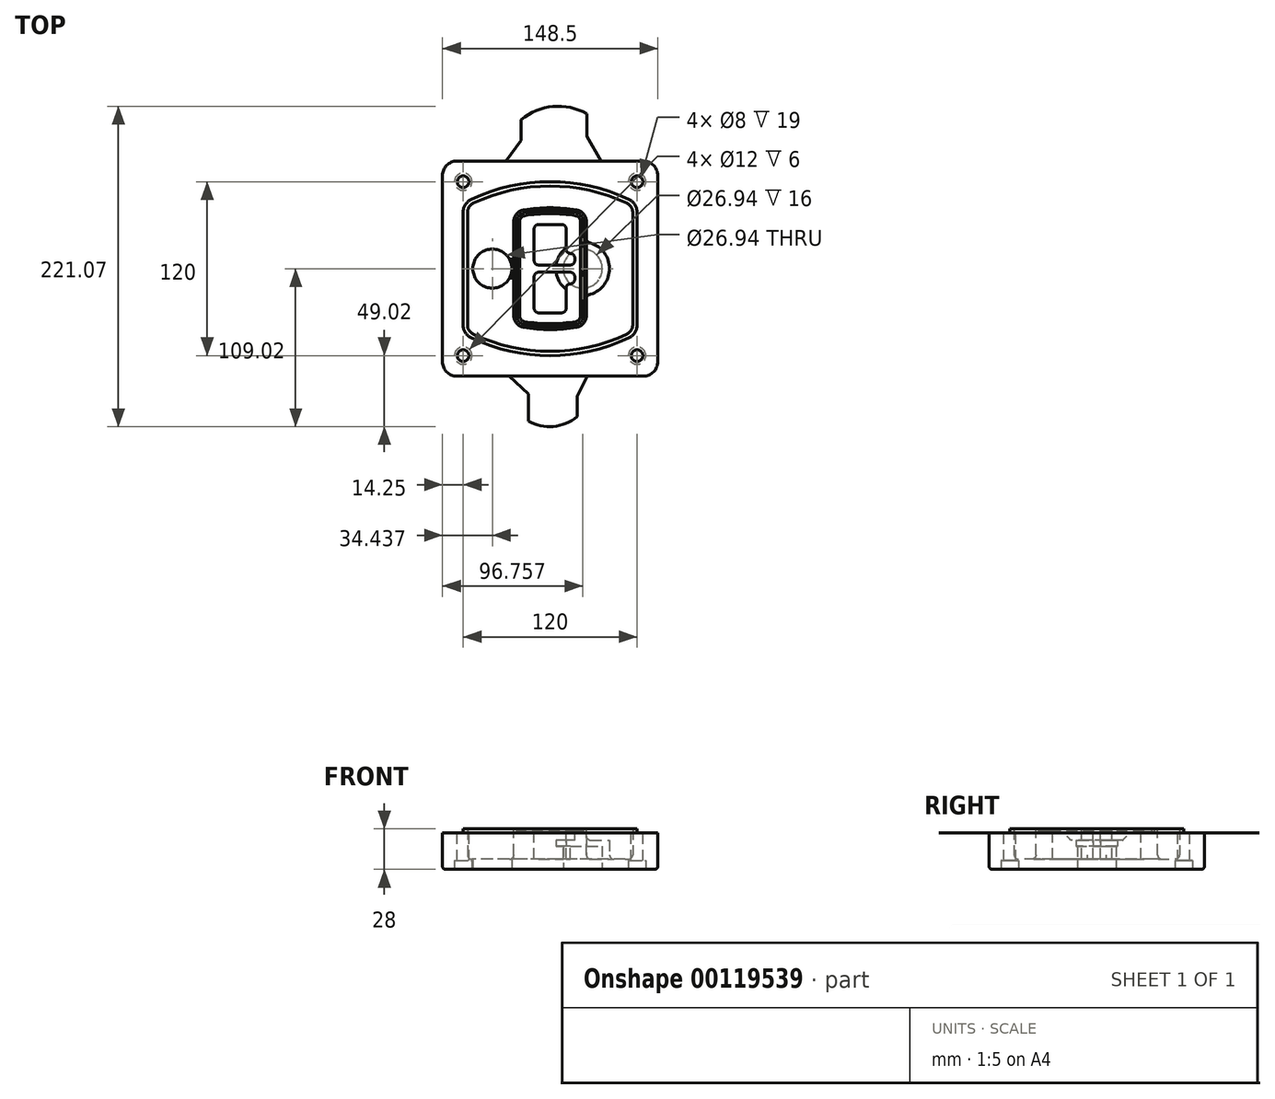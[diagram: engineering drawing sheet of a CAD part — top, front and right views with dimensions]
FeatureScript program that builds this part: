
annotation { "Feature Type Name" : "Feature", "Feature Type Description" : "" }
export const myFeature = defineFeature(function(context is Context, id is Id, definition is map)
    precondition{}
    {
        {
            var Q0;
            Q0=qCreatedBy(makeId("Top.planeOp"),FACE);
            var sketch = newSketch(context, id + "F0", { "sketchPlane" : qUnion([Q0])});
            skPoint(sketch, "E0.rect.middle", {"position": v(0, 0) * mm});
            skLineSegment(sketch, "E1.bottom", {"start": v(-64.25, -74.25) * mm, "end": v(64.25, -74.25) * mm});
            skLineSegment(sketch, "E1.top", {"start": v(-64.25, 74.25) * mm, "end": v(64.25, 74.25) * mm});
            skLineSegment(sketch, "E1.left", {"start": v(-74.25, -64.25) * mm, "end": v(-74.25, 64.25) * mm});
            skLineSegment(sketch, "E1.right", {"start": v(74.25, -64.25) * mm, "end": v(74.25, 64.25) * mm});
            skLineSegment(sketch, "E2", {"start": v(-74.25, 74.25) * mm, "end": v(74.25, -74.25) * mm, "construction": true});
            skLineSegment(sketch, "E3", {"start": v(74.25, 74.25) * mm, "end": v(-74.25, -74.25) * mm, "construction": true});
            skCircle(sketch, "E4", {"center": v(-60, 60) * mm, "radius": 4 * mm});
            skCircle(sketch, "E5", {"center": v(60, 60) * mm, "radius": 4 * mm});
            skCircle(sketch, "E6", {"center": v(60, -60) * mm, "radius": 4 * mm});
            skCircle(sketch, "E7", {"center": v(-60, -60) * mm, "radius": 4 * mm});
            skLineSegment(sketch, "E8", {"start": v(-60, 60) * mm, "end": v(60, 60) * mm, "construction": true});
            skLineSegment(sketch, "E9", {"start": v(60, 60) * mm, "end": v(60, -60) * mm, "construction": true});
            skLineSegment(sketch, "E10", {"start": v(60, -60) * mm, "end": v(-60, -60) * mm, "construction": true});
            skLineSegment(sketch, "E11", {"start": v(-60, -60) * mm, "end": v(-60, 60) * mm, "construction": true});
            skLineSegment(sketch, "E12", {"start": v(-60, 38.83) * mm, "end": v(-60, -38.83) * mm});
            skLineSegment(sketch, "E13", {"start": v(60, 38.83) * mm, "end": v(60, -38.83) * mm});
            skArc(sketch, "E14", {"start": v(54.26, 47.88) * mm, "mid": v(0, 60) * mm, "end": v(-54.26, 47.88) * mm});
            skArc(sketch, "E15", {"start": v(-54.26, -47.88) * mm, "mid": v(0, -60) * mm, "end": v(54.26, -47.88) * mm});
            skLineSegment(sketch, "E16", {"start": v(-60, 0) * mm, "end": v(60, 0) * mm, "construction": true});
            skPoint(sketch, "E17.visualSharp", {"position": v(-60, -45) * mm});
            skArc(sketch, "E17.filletArc", {"start": v(-60, -38.83) * mm, "mid": v(-58.44, -44.2) * mm, "end": v(-54.26, -47.88) * mm});
            skPoint(sketch, "E18.visualSharp", {"position": v(-60, 45) * mm});
            skArc(sketch, "E18.filletArc", {"start": v(-54.26, 47.88) * mm, "mid": v(-58.44, 44.2) * mm, "end": v(-60, 38.83) * mm});
            skPoint(sketch, "E19.visualSharp", {"position": v(60, 45) * mm});
            skArc(sketch, "E19.filletArc", {"start": v(60, 38.83) * mm, "mid": v(58.44, 44.2) * mm, "end": v(54.26, 47.88) * mm});
            skPoint(sketch, "E20.visualSharp", {"position": v(60, -45) * mm});
            skArc(sketch, "E20.filletArc", {"start": v(54.26, -47.88) * mm, "mid": v(58.44, -44.2) * mm, "end": v(60, -38.83) * mm});
            skPoint(sketch, "E21.visualSharp", {"position": v(-74.25, 74.25) * mm});
            skArc(sketch, "E21.filletArc", {"start": v(-64.25, 74.25) * mm, "mid": v(-71.32, 71.32) * mm, "end": v(-74.25, 64.25) * mm});
            skPoint(sketch, "E22.visualSharp", {"position": v(74.25, 74.25) * mm});
            skArc(sketch, "E22.filletArc", {"start": v(74.25, 64.25) * mm, "mid": v(71.32, 71.32) * mm, "end": v(64.25, 74.25) * mm});
            skPoint(sketch, "E23.visualSharp", {"position": v(74.25, -74.25) * mm});
            skArc(sketch, "E23.filletArc", {"start": v(64.25, -74.25) * mm, "mid": v(71.32, -71.32) * mm, "end": v(74.25, -64.25) * mm});
            skPoint(sketch, "E24.visualSharp", {"position": v(-74.25, -74.25) * mm});
            skArc(sketch, "E24.filletArc", {"start": v(-74.25, -64.25) * mm, "mid": v(-71.32, -71.32) * mm, "end": v(-64.25, -74.25) * mm});
            skArc(sketch, "E25.0", {"start": v(57, 38.83) * mm, "mid": v(55.9, 42.58) * mm, "end": v(52.98, 45.17) * mm});
            skLineSegment(sketch, "E25.1", {"start": v(57, 38.83) * mm, "end": v(57, -38.83) * mm});
            skArc(sketch, "E25.2", {"start": v(52.98, -45.17) * mm, "mid": v(55.9, -42.58) * mm, "end": v(57, -38.83) * mm});
            skArc(sketch, "E25.3", {"start": v(-52.98, -45.17) * mm, "mid": v(0, -57) * mm, "end": v(52.98, -45.17) * mm});
            skArc(sketch, "E25.4", {"start": v(-57, -38.83) * mm, "mid": v(-55.9, -42.58) * mm, "end": v(-52.98, -45.17) * mm});
            skArc(sketch, "E25.5", {"start": v(52.98, 45.17) * mm, "mid": v(0, 57) * mm, "end": v(-52.98, 45.17) * mm});
            skLineSegment(sketch, "E25.6", {"start": v(-57, 38.83) * mm, "end": v(-57, -38.83) * mm});
            skArc(sketch, "E25.7", {"start": v(-52.98, 45.17) * mm, "mid": v(-55.9, 42.58) * mm, "end": v(-57, 38.83) * mm});
            skArc(sketch, "E26.0", {"start": v(-55.96, 51.5) * mm, "mid": v(-61.82, 46.33) * mm, "end": v(-64, 38.83) * mm});
            skArc(sketch, "E26.1", {"start": v(55.96, 51.5) * mm, "mid": v(0, 64) * mm, "end": v(-55.96, 51.5) * mm});
            skArc(sketch, "E26.2", {"start": v(64, 38.83) * mm, "mid": v(61.82, 46.33) * mm, "end": v(55.96, 51.5) * mm});
            skLineSegment(sketch, "E26.3", {"start": v(64, 38.83) * mm, "end": v(64, -38.83) * mm});
            skArc(sketch, "E26.4", {"start": v(55.96, -51.5) * mm, "mid": v(61.82, -46.33) * mm, "end": v(64, -38.83) * mm});
            skLineSegment(sketch, "E26.5", {"start": v(-64, 38.83) * mm, "end": v(-64, -38.83) * mm});
            skArc(sketch, "E26.6", {"start": v(-55.96, -51.5) * mm, "mid": v(0, -64) * mm, "end": v(55.96, -51.5) * mm});
            skArc(sketch, "E26.7", {"start": v(-64, -38.83) * mm, "mid": v(-61.82, -46.33) * mm, "end": v(-55.96, -51.5) * mm});
            skSolve(sketch);
        }
        {
            var Q0;
            Q0=makeQuery(id+"F0.imprint","IMPRINT",FACE,{"disambiguationData":[TD([[makeQuery(id+"F0.imprint","IMPRINT",EDGE,{"derivedFrom":sQuery(id+"F0.wireOp",EDGE,"E1.bottom")}),1.0]])]});
            var Q1;
            Q1=makeQuery(id+"F0.imprint","IMPRINT",FACE,{"disambiguationData":[TD([[makeQuery(id+"F0.imprint","IMPRINT",EDGE,{"derivedFrom":sQuery(id+"F0.wireOp",EDGE,"E12")}),1.0]])]});
            var Q2;
            Q2=makeQuery(id+"F0.imprint","IMPRINT",FACE,{"disambiguationData":[TD([[makeQuery(id+"F0.imprint","IMPRINT",EDGE,{"derivedFrom":sQuery(id+"F0.wireOp",EDGE,"E25.0")}),1.0]])]});
            var Q3;
            Q3=makeQuery(id+"F0.imprint","IMPRINT",FACE,{"disambiguationData":[TD([[makeQuery(id+"F0.imprint","IMPRINT",EDGE,{"derivedFrom":sQuery(id+"F0.wireOp",EDGE,"E12")}),-1.0]])]});
            extrude(context, id + "F1", {"entities" : qUnion([Q0, Q1, Q2, Q3]), "oppositeDirection" : true, "depth" : 25 * mm});
        }
        {
            var Q0;
            Q0=makeQuery(id+"F0.imprint","IMPRINT",FACE,{"disambiguationData":[TD([[makeQuery(id+"F0.imprint","IMPRINT",EDGE,{"derivedFrom":sQuery(id+"F0.wireOp",EDGE,"E12")}),1.0]])]});
            extrude(context, id + "F2", {"entities" : qUnion([Q0]), "operationType" : NewBodyOperationType.ADD, "depth" : 3 * mm});
        }
        {
            var Q0;
            Q0=makeQuery(id+"F0.imprint","IMPRINT",FACE,{"disambiguationData":[TD([[makeQuery(id+"F0.imprint","IMPRINT",EDGE,{"derivedFrom":sQuery(id+"F0.wireOp",EDGE,"E25.0")}),1.0]])]});
            extrude(context, id + "F3", {"entities" : qUnion([Q0]), "operationType" : NewBodyOperationType.REMOVE, "oppositeDirection" : true, "depth" : 18 * mm});
        }
        {
            var Q0;
            Q0=makeQuery(id+"F2.opExtrude","CAP_FACE",FACE,{"disambiguationData":[OSD([sQuery(id+"F0.wireOp",EDGE,"E12"),sQuery(id+"F0.wireOp",EDGE,"E13"),sQuery(id+"F0.wireOp",EDGE,"E14"),sQuery(id+"F0.wireOp",EDGE,"E15"),sQuery(id+"F0.wireOp",EDGE,"E17.filletArc"),sQuery(id+"F0.wireOp",EDGE,"E18.filletArc"),sQuery(id+"F0.wireOp",EDGE,"E19.filletArc"),sQuery(id+"F0.wireOp",EDGE,"E20.filletArc"),sQuery(id+"F0.wireOp",EDGE,"E25.0"),sQuery(id+"F0.wireOp",EDGE,"E25.1"),sQuery(id+"F0.wireOp",EDGE,"E25.2"),sQuery(id+"F0.wireOp",EDGE,"E25.3"),sQuery(id+"F0.wireOp",EDGE,"E25.4"),sQuery(id+"F0.wireOp",EDGE,"E25.5"),sQuery(id+"F0.wireOp",EDGE,"E25.6"),sQuery(id+"F0.wireOp",EDGE,"E25.7")])],"isStart":false});
            var sketch = newSketch(context, id + "F4", { "sketchPlane" : qUnion([Q0])});
            skArc(sketch, "E27.0", {"start": v(-18.34, -40.45) * mm, "mid": v(0, -42) * mm, "end": v(18.34, -40.45) * mm});
            skArc(sketch, "E28.0", {"start": v(18.34, 40.45) * mm, "mid": v(0, 42) * mm, "end": v(-18.34, 40.45) * mm});
            skLineSegment(sketch, "E29", {"start": v(-25, 32.57) * mm, "end": v(-25, -32.57) * mm});
            skLineSegment(sketch, "E30", {"start": v(25, 32.57) * mm, "end": v(25, -32.57) * mm});
            skLineSegment(sketch, "E31", {"start": v(-25, 39.1) * mm, "end": v(25, 39.1) * mm, "construction": true});
            skLineSegment(sketch, "E32", {"start": v(-25, -39.1) * mm, "end": v(25, -39.1) * mm, "construction": true});
            skPoint(sketch, "E33.visualSharp", {"position": v(-25, 39.1) * mm});
            skArc(sketch, "E33.filletArc", {"start": v(-18.34, 40.45) * mm, "mid": v(-23.11, 37.73) * mm, "end": v(-25, 32.57) * mm});
            skPoint(sketch, "E34.visualSharp", {"position": v(25, 39.1) * mm});
            skArc(sketch, "E34.filletArc", {"start": v(25, 32.57) * mm, "mid": v(23.11, 37.73) * mm, "end": v(18.34, 40.45) * mm});
            skPoint(sketch, "E35.visualSharp", {"position": v(25, -39.1) * mm});
            skArc(sketch, "E35.filletArc", {"start": v(18.34, -40.45) * mm, "mid": v(23.11, -37.73) * mm, "end": v(25, -32.57) * mm});
            skPoint(sketch, "E36.visualSharp", {"position": v(-25, -39.1) * mm});
            skArc(sketch, "E36.filletArc", {"start": v(-25, -32.57) * mm, "mid": v(-23.11, -37.73) * mm, "end": v(-18.34, -40.45) * mm});
            skArc(sketch, "E37.0", {"start": v(52.98, 45.17) * mm, "mid": v(0, 57) * mm, "end": v(-52.98, 45.17) * mm});
            skArc(sketch, "E37.1", {"start": v(-52.98, 45.17) * mm, "mid": v(-55.9, 42.58) * mm, "end": v(-57, 38.83) * mm});
            skLineSegment(sketch, "E37.2", {"start": v(-57, 38.83) * mm, "end": v(-57, -38.83) * mm});
            skArc(sketch, "E37.3", {"start": v(-57, -38.83) * mm, "mid": v(-55.9, -42.58) * mm, "end": v(-52.98, -45.17) * mm});
            skArc(sketch, "E37.4", {"start": v(-52.98, -45.17) * mm, "mid": v(0, -57) * mm, "end": v(52.98, -45.17) * mm});
            skArc(sketch, "E37.5", {"start": v(52.98, -45.17) * mm, "mid": v(55.9, -42.58) * mm, "end": v(57, -38.83) * mm});
            skLineSegment(sketch, "E37.6", {"start": v(57, 38.83) * mm, "end": v(57, -38.83) * mm});
            skArc(sketch, "E37.7", {"start": v(57, 38.83) * mm, "mid": v(55.9, 42.58) * mm, "end": v(52.98, 45.17) * mm});
            skLineSegment(sketch, "E38.0", {"start": v(23, 32.57) * mm, "end": v(23, -32.57) * mm});
            skArc(sketch, "E38.1", {"start": v(18, -38.48) * mm, "mid": v(21.58, -36.44) * mm, "end": v(23, -32.57) * mm});
            skArc(sketch, "E38.2", {"start": v(-18, -38.48) * mm, "mid": v(0, -40) * mm, "end": v(18, -38.48) * mm});
            skArc(sketch, "E38.3", {"start": v(-23, -32.57) * mm, "mid": v(-21.58, -36.44) * mm, "end": v(-18, -38.48) * mm});
            skLineSegment(sketch, "E38.4", {"start": v(-23, 32.57) * mm, "end": v(-23, -32.57) * mm});
            skArc(sketch, "E38.5", {"start": v(23, 32.57) * mm, "mid": v(21.58, 36.44) * mm, "end": v(18, 38.48) * mm});
            skArc(sketch, "E38.6", {"start": v(-18, 38.48) * mm, "mid": v(-21.58, 36.44) * mm, "end": v(-23, 32.57) * mm});
            skArc(sketch, "E38.7", {"start": v(18, 38.48) * mm, "mid": v(0, 40) * mm, "end": v(-18, 38.48) * mm});
            skArc(sketch, "E39.0", {"start": v(21, 32.57) * mm, "mid": v(20.06, 35.15) * mm, "end": v(17.67, 36.5) * mm});
            skLineSegment(sketch, "E39.1", {"start": v(21, 32.57) * mm, "end": v(21, -32.57) * mm});
            skArc(sketch, "E39.2", {"start": v(17.67, -36.5) * mm, "mid": v(20.06, -35.15) * mm, "end": v(21, -32.57) * mm});
            skArc(sketch, "E39.3", {"start": v(-17.67, -36.5) * mm, "mid": v(0, -38) * mm, "end": v(17.67, -36.5) * mm});
            skArc(sketch, "E39.4", {"start": v(-21, -32.57) * mm, "mid": v(-20.06, -35.15) * mm, "end": v(-17.67, -36.5) * mm});
            skArc(sketch, "E39.5", {"start": v(17.67, 36.5) * mm, "mid": v(0, 38) * mm, "end": v(-17.67, 36.5) * mm});
            skLineSegment(sketch, "E39.6", {"start": v(-21, 32.57) * mm, "end": v(-21, -32.57) * mm});
            skArc(sketch, "E39.7", {"start": v(-17.67, 36.5) * mm, "mid": v(-20.06, 35.15) * mm, "end": v(-21, 32.57) * mm});
            skLineSegment(sketch, "E40", {"start": v(-25, 0) * mm, "end": v(25, 0) * mm, "construction": true});
            skLineSegment(sketch, "E41", {"start": v(-11, 5.5) * mm, "end": v(-11, 27.5) * mm});
            skLineSegment(sketch, "E42", {"start": v(-8, 30.5) * mm, "end": v(8, 30.5) * mm});
            skLineSegment(sketch, "E43", {"start": v(11, 27.5) * mm, "end": v(11, 13.5) * mm});
            skLineSegment(sketch, "E44", {"start": v(14, 10.5) * mm, "end": v(14, 10.5) * mm});
            skLineSegment(sketch, "E45", {"start": v(17, 7.5) * mm, "end": v(17, 5.5) * mm});
            skLineSegment(sketch, "E46", {"start": v(14, 2.5) * mm, "end": v(-8, 2.5) * mm});
            skPoint(sketch, "E47.visualSharp", {"position": v(-11, 30.5) * mm});
            skArc(sketch, "E47.filletArc", {"start": v(-8, 30.5) * mm, "mid": v(-10.12, 29.62) * mm, "end": v(-11, 27.5) * mm});
            skPoint(sketch, "E48.visualSharp", {"position": v(11, 30.5) * mm});
            skArc(sketch, "E48.filletArc", {"start": v(11, 27.5) * mm, "mid": v(10.12, 29.62) * mm, "end": v(8, 30.5) * mm});
            skPoint(sketch, "E49.visualSharp", {"position": v(11, 10.5) * mm});
            skArc(sketch, "E49.filletArc", {"start": v(11, 13.5) * mm, "mid": v(11.88, 11.38) * mm, "end": v(14, 10.5) * mm});
            skPoint(sketch, "E50.visualSharp", {"position": v(17, 10.5) * mm});
            skArc(sketch, "E50.filletArc", {"start": v(17, 7.5) * mm, "mid": v(16.12, 9.62) * mm, "end": v(14, 10.5) * mm});
            skPoint(sketch, "E51.visualSharp", {"position": v(17, 2.5) * mm});
            skArc(sketch, "E51.filletArc", {"start": v(14, 2.5) * mm, "mid": v(16.12, 3.38) * mm, "end": v(17, 5.5) * mm});
            skPoint(sketch, "E52.visualSharp", {"position": v(-11, 2.5) * mm});
            skArc(sketch, "E52.filletArc", {"start": v(-11, 5.5) * mm, "mid": v(-10.12, 3.38) * mm, "end": v(-8, 2.5) * mm});
            skLineSegment(sketch, "E53.0.MirrorCS", {"start": v(14, -2.5) * mm, "end": v(-8, -2.5) * mm});
            skArc(sketch, "E54.0.MirrorCS", {"start": v(-11, -5.5) * mm, "mid": v(-10.12, -3.38) * mm, "end": v(-8, -2.5) * mm});
            skLineSegment(sketch, "E55.0.MirrorCS", {"start": v(-11, -5.5) * mm, "end": v(-11, -27.5) * mm});
            skArc(sketch, "E56.0.MirrorCS", {"start": v(-8, -30.5) * mm, "mid": v(-10.12, -29.62) * mm, "end": v(-11, -27.5) * mm});
            skLineSegment(sketch, "E57.0.MirrorCS", {"start": v(-8, -30.5) * mm, "end": v(8, -30.5) * mm});
            skArc(sketch, "E58.0.MirrorCS", {"start": v(11, -27.5) * mm, "mid": v(10.12, -29.62) * mm, "end": v(8, -30.5) * mm});
            skLineSegment(sketch, "E59.0.MirrorCS", {"start": v(11, -27.5) * mm, "end": v(11, -13.5) * mm});
            skArc(sketch, "E60.0.MirrorCS", {"start": v(11, -13.5) * mm, "mid": v(11.88, -11.38) * mm, "end": v(14, -10.5) * mm});
            skArc(sketch, "E61.0.MirrorCS", {"start": v(17, -7.5) * mm, "mid": v(16.12, -9.62) * mm, "end": v(14, -10.5) * mm});
            skLineSegment(sketch, "E62.0.MirrorCS", {"start": v(17, -7.5) * mm, "end": v(17, -5.5) * mm});
            skArc(sketch, "E63.0.MirrorCS", {"start": v(14, -2.5) * mm, "mid": v(16.12, -3.38) * mm, "end": v(17, -5.5) * mm});
            skSolve(sketch);
        }
        {
            var Q0;
            Q0=makeQuery(id+"F4.imprint","IMPRINT",FACE,{"disambiguationData":[TD([[makeQuery(id+"F4.imprint","IMPRINT",EDGE,{"derivedFrom":sQuery(id+"F4.wireOp",EDGE,"E27.0")}),1.0]])]});
            var Q1;
            Q1=makeQuery(id+"F4.imprint","IMPRINT",FACE,{"disambiguationData":[TD([[makeQuery(id+"F4.imprint","IMPRINT",EDGE,{"derivedFrom":sQuery(id+"F4.wireOp",EDGE,"E38.0")}),-1.0]])]});
            var Q2;
            Q2=makeQuery(id+"F4.imprint","IMPRINT",FACE,{"disambiguationData":[TD([[makeQuery(id+"F4.imprint","IMPRINT",EDGE,{"derivedFrom":sQuery(id+"F4.wireOp",EDGE,"E39.0")}),1.0]])]});
            extrude(context, id + "F5", {"entities" : qUnion([Q0, Q1, Q2]), "operationType" : NewBodyOperationType.ADD, "endBound" : BoundingType.UP_TO_NEXT, "oppositeDirection" : true, "depth" : 25 * mm});
        }
        {
            var Q0;
            Q0=makeQuery(id+"F4.imprint","IMPRINT",FACE,{"disambiguationData":[TD([[makeQuery(id+"F4.imprint","IMPRINT",EDGE,{"derivedFrom":sQuery(id+"F4.wireOp",EDGE,"E38.0")}),-1.0]])]});
            extrude(context, id + "F6", {"entities" : qUnion([Q0]), "operationType" : NewBodyOperationType.REMOVE, "oppositeDirection" : true, "depth" : 2 * mm});
        }
        {
            var Q0;
            Q0=makeQuery(id+"F1.opExtrude","CAP_FACE",FACE,{"disambiguationData":[OSD([sQuery(id+"F0.wireOp",EDGE,"E1.bottom"),sQuery(id+"F0.wireOp",EDGE,"E1.top"),sQuery(id+"F0.wireOp",EDGE,"E1.left"),sQuery(id+"F0.wireOp",EDGE,"E1.right"),sQuery(id+"F0.wireOp",EDGE,"E4"),sQuery(id+"F0.wireOp",EDGE,"E5"),sQuery(id+"F0.wireOp",EDGE,"E6"),sQuery(id+"F0.wireOp",EDGE,"E7"),sQuery(id+"F0.wireOp",EDGE,"E21.filletArc"),sQuery(id+"F0.wireOp",EDGE,"E22.filletArc"),sQuery(id+"F0.wireOp",EDGE,"E23.filletArc"),sQuery(id+"F0.wireOp",EDGE,"E24.filletArc")])],"isStart":false});
            var sketch = newSketch(context, id + "F7", { "sketchPlane" : qUnion([Q0])});
            skCircle(sketch, "E64", {"center": v(22.5, 0) * mm, "radius": 13.47 * mm});
            skCircle(sketch, "E65", {"center": v(-39.81, 0) * mm, "radius": 13.47 * mm});
            skLineSegment(sketch, "E66", {"start": v(74.25, 0) * mm, "end": v(-74.25, 0) * mm});
            skCircle(sketch, "E67", {"center": v(22.5, 0) * mm, "radius": 18.47 * mm});
            skCircle(sketch, "E68", {"center": v(60, -60) * mm, "radius": 6 * mm});
            skCircle(sketch, "E69", {"center": v(-60, -60) * mm, "radius": 6 * mm});
            skCircle(sketch, "E70", {"center": v(-60, 60) * mm, "radius": 6 * mm});
            skCircle(sketch, "E71", {"center": v(60, 60) * mm, "radius": 6 * mm});
            skSolve(sketch);
        }
        {
            var Q0;
            {var subQ1=sQuery(id+"F7.wireOp",EDGE,"E66");var subQ4=sQuery(id+"F7.wireOp",EDGE,"E64");var subQ6=makeQuery(id+"F7.imprint","INTERSECT",VERTEX,{"disambiguationData":[OD(0.0)],"derivedFrom":[subQ4,subQ1]});Q0=makeQuery(id+"F7.imprint","IMPRINT",FACE,{"disambiguationData":[TD([[makeQuery(id+"F7.imprint","IMPRINT",EDGE,{"disambiguationData":[TD([[subQ6,-1.0]])],"derivedFrom":subQ4}),-1.0]])]});}
            var Q1;
            {var subQ0=sQuery(id+"F7.wireOp",EDGE,"E66");var subQ1=sQuery(id+"F7.wireOp",EDGE,"E64");var subQ3=makeQuery(id+"F7.imprint","INTERSECT",VERTEX,{"disambiguationData":[OD(0.0)],"derivedFrom":[subQ1,subQ0]});Q1=makeQuery(id+"F7.imprint","IMPRINT",FACE,{"disambiguationData":[TD([[makeQuery(id+"F7.imprint","IMPRINT",EDGE,{"disambiguationData":[TD([[subQ3,-1.0]])],"derivedFrom":subQ1}),1.0]])]});}
            var Q2;
            {var subQ0=sQuery(id+"F7.wireOp",EDGE,"E66");var subQ1=sQuery(id+"F7.wireOp",EDGE,"E64");var subQ3=makeQuery(id+"F7.imprint","INTERSECT",VERTEX,{"disambiguationData":[OD(0.0)],"derivedFrom":[subQ1,subQ0]});Q2=makeQuery(id+"F7.imprint","IMPRINT",FACE,{"disambiguationData":[TD([[makeQuery(id+"F7.imprint","IMPRINT",EDGE,{"disambiguationData":[TD([[subQ3,1.0]])],"derivedFrom":subQ1}),1.0]])]});}
            var Q3;
            {var subQ1=sQuery(id+"F7.wireOp",EDGE,"E66");var subQ4=sQuery(id+"F7.wireOp",EDGE,"E64");var subQ6=makeQuery(id+"F7.imprint","INTERSECT",VERTEX,{"disambiguationData":[OD(0.0)],"derivedFrom":[subQ4,subQ1]});Q3=makeQuery(id+"F7.imprint","IMPRINT",FACE,{"disambiguationData":[TD([[makeQuery(id+"F7.imprint","IMPRINT",EDGE,{"disambiguationData":[TD([[subQ6,1.0]])],"derivedFrom":subQ4}),-1.0]])]});}
            extrude(context, id + "F8", {"entities" : qUnion([Q0, Q1, Q2, Q3]), "operationType" : NewBodyOperationType.ADD, "oppositeDirection" : true, "depth" : 20 * mm});
        }
        {
            var Q0;
            {var subQ0=sQuery(id+"F7.wireOp",EDGE,"E66");var subQ1=sQuery(id+"F7.wireOp",EDGE,"E64");var subQ3=makeQuery(id+"F7.imprint","INTERSECT",VERTEX,{"disambiguationData":[OD(0.0)],"derivedFrom":[subQ1,subQ0]});Q0=makeQuery(id+"F7.imprint","IMPRINT",FACE,{"disambiguationData":[TD([[makeQuery(id+"F7.imprint","IMPRINT",EDGE,{"disambiguationData":[TD([[subQ3,-1.0]])],"derivedFrom":subQ1}),1.0]])]});}
            var Q1;
            {var subQ0=sQuery(id+"F7.wireOp",EDGE,"E66");var subQ1=sQuery(id+"F7.wireOp",EDGE,"E64");var subQ3=makeQuery(id+"F7.imprint","INTERSECT",VERTEX,{"disambiguationData":[OD(0.0)],"derivedFrom":[subQ1,subQ0]});Q1=makeQuery(id+"F7.imprint","IMPRINT",FACE,{"disambiguationData":[TD([[makeQuery(id+"F7.imprint","IMPRINT",EDGE,{"disambiguationData":[TD([[subQ3,1.0]])],"derivedFrom":subQ1}),1.0]])]});}
            extrude(context, id + "F9", {"entities" : qUnion([Q0, Q1]), "operationType" : NewBodyOperationType.REMOVE, "oppositeDirection" : true, "depth" : 16 * mm});
        }
        {
            var Q0;
            {var subQ0=sQuery(id+"F7.wireOp",EDGE,"E66");var subQ1=sQuery(id+"F7.wireOp",EDGE,"E65");var subQ3=makeQuery(id+"F7.imprint","INTERSECT",VERTEX,{"disambiguationData":[OD(0.0)],"derivedFrom":[subQ1,subQ0]});Q0=makeQuery(id+"F7.imprint","IMPRINT",FACE,{"disambiguationData":[TD([[makeQuery(id+"F7.imprint","IMPRINT",EDGE,{"disambiguationData":[TD([[subQ3,-1.0]])],"derivedFrom":subQ1}),1.0]])]});}
            var Q1;
            {var subQ0=sQuery(id+"F7.wireOp",EDGE,"E66");var subQ1=sQuery(id+"F7.wireOp",EDGE,"E65");var subQ3=makeQuery(id+"F7.imprint","INTERSECT",VERTEX,{"disambiguationData":[OD(0.0)],"derivedFrom":[subQ1,subQ0]});Q1=makeQuery(id+"F7.imprint","IMPRINT",FACE,{"disambiguationData":[TD([[makeQuery(id+"F7.imprint","IMPRINT",EDGE,{"disambiguationData":[TD([[subQ3,1.0]])],"derivedFrom":subQ1}),1.0]])]});}
            extrude(context, id + "F10", {"entities" : qUnion([Q0, Q1]), "operationType" : NewBodyOperationType.REMOVE, "oppositeDirection" : true, "depth" : 25 * mm});
        }
        {
            var Q0;
            Q0=makeQuery(id+"F7.imprint","IMPRINT",FACE,{"disambiguationData":[TD([[makeQuery(id+"F7.imprint","IMPRINT",EDGE,{"derivedFrom":sQuery(id+"F7.wireOp",EDGE,"E68")}),1.0]])]});
            var Q1;
            Q1=makeQuery(id+"F7.imprint","IMPRINT",FACE,{"disambiguationData":[TD([[makeQuery(id+"F7.imprint","IMPRINT",EDGE,{"derivedFrom":makeQuery(id+"F1.opExtrude","CAP_EDGE",EDGE,{"disambiguationData":[OSD([sQuery(id+"F0.wireOp",EDGE,"E5")])],"isStart":false})}),-1.0]])]});
            var Q2;
            Q2=makeQuery(id+"F7.imprint","IMPRINT",FACE,{"disambiguationData":[TD([[makeQuery(id+"F7.imprint","IMPRINT",EDGE,{"derivedFrom":sQuery(id+"F7.wireOp",EDGE,"E69")}),1.0]])]});
            var Q3;
            Q3=makeQuery(id+"F7.imprint","IMPRINT",FACE,{"disambiguationData":[TD([[makeQuery(id+"F7.imprint","IMPRINT",EDGE,{"derivedFrom":makeQuery(id+"F1.opExtrude","CAP_EDGE",EDGE,{"disambiguationData":[OSD([sQuery(id+"F0.wireOp",EDGE,"E4")])],"isStart":false})}),-1.0]])]});
            var Q4;
            Q4=makeQuery(id+"F7.imprint","IMPRINT",FACE,{"disambiguationData":[TD([[makeQuery(id+"F7.imprint","IMPRINT",EDGE,{"derivedFrom":sQuery(id+"F7.wireOp",EDGE,"E70")}),1.0]])]});
            var Q5;
            Q5=makeQuery(id+"F7.imprint","IMPRINT",FACE,{"disambiguationData":[TD([[makeQuery(id+"F7.imprint","IMPRINT",EDGE,{"derivedFrom":makeQuery(id+"F1.opExtrude","CAP_EDGE",EDGE,{"disambiguationData":[OSD([sQuery(id+"F0.wireOp",EDGE,"E7")])],"isStart":false})}),-1.0]])]});
            var Q6;
            Q6=makeQuery(id+"F7.imprint","IMPRINT",FACE,{"disambiguationData":[TD([[makeQuery(id+"F7.imprint","IMPRINT",EDGE,{"derivedFrom":sQuery(id+"F7.wireOp",EDGE,"E71")}),1.0]])]});
            var Q7;
            Q7=makeQuery(id+"F7.imprint","IMPRINT",FACE,{"disambiguationData":[TD([[makeQuery(id+"F7.imprint","IMPRINT",EDGE,{"derivedFrom":makeQuery(id+"F1.opExtrude","CAP_EDGE",EDGE,{"disambiguationData":[OSD([sQuery(id+"F0.wireOp",EDGE,"E6")])],"isStart":false})}),-1.0]])]});
            extrude(context, id + "F11", {"entities" : qUnion([Q0, Q1, Q2, Q3, Q4, Q5, Q6, Q7]), "operationType" : NewBodyOperationType.REMOVE, "oppositeDirection" : true, "depth" : 6 * mm});
        }
        {
            var Q0;
            Q0=makeQuery(id+"F9.boolean.opBoolean","COPY",FACE,{"derivedFrom":makeQuery(id+"F9.opExtrude","CAP_FACE",FACE,{"disambiguationData":[OSD([sQuery(id+"F7.wireOp",EDGE,"E64")])],"isStart":false})});
            var sketch = newSketch(context, id + "F12", { "sketchPlane" : qUnion([Q0])});
            skArc(sketch, "E72.0", {"start": v(11, 14.45) * mm, "mid": v(6.45, 9.13) * mm, "end": v(4.2, 2.5) * mm});
            skArc(sketch, "E72.1", {"start": v(4.2, -2.5) * mm, "mid": v(6.45, -9.13) * mm, "end": v(11, -14.45) * mm});
            skLineSegment(sketch, "E73", {"start": v(4.2, -2.5) * mm, "end": v(14, -2.5) * mm});
            skLineSegment(sketch, "E74.0", {"start": v(14, 2.5) * mm, "end": v(4.2, 2.5) * mm});
            skArc(sketch, "E74.1", {"start": v(14, 2.5) * mm, "mid": v(16.12, 3.38) * mm, "end": v(17, 5.5) * mm});
            skLineSegment(sketch, "E74.2", {"start": v(17, 7.5) * mm, "end": v(17, 5.5) * mm});
            skArc(sketch, "E74.3", {"start": v(17, 7.5) * mm, "mid": v(16.12, 9.62) * mm, "end": v(14, 10.5) * mm});
            skArc(sketch, "E74.4", {"start": v(11, 13.5) * mm, "mid": v(11.88, 11.38) * mm, "end": v(14, 10.5) * mm});
            skLineSegment(sketch, "E74.5", {"start": v(11, 14.45) * mm, "end": v(11, 13.5) * mm});
            skLineSegment(sketch, "E74.7", {"start": v(14, -2.5) * mm, "end": v(4.2, -2.5) * mm});
            skArc(sketch, "E74.8", {"start": v(14, -2.5) * mm, "mid": v(16.12, -3.38) * mm, "end": v(17, -5.5) * mm});
            skLineSegment(sketch, "E74.9", {"start": v(17, -7.5) * mm, "end": v(17, -5.5) * mm});
            skArc(sketch, "E74.10", {"start": v(17, -7.5) * mm, "mid": v(16.12, -9.62) * mm, "end": v(14, -10.5) * mm});
            skArc(sketch, "E74.11", {"start": v(11, -13.5) * mm, "mid": v(11.88, -11.38) * mm, "end": v(14, -10.5) * mm});
            skLineSegment(sketch, "E74.12", {"start": v(11, -14.45) * mm, "end": v(11, -13.5) * mm});
            skPoint(sketch, "E75.orphan", {"position": v(11, -27.5) * mm});
            skPoint(sketch, "E76.orphan", {"position": v(-8, -2.5) * mm});
            skPoint(sketch, "E77.orphan", {"position": v(-8, 2.5) * mm});
            skPoint(sketch, "E78.orphan", {"position": v(11, 27.5) * mm});
            skSolve(sketch);
        }
        {
            var Q0;
            {var subQ7=sQuery(id+"F12.wireOp",EDGE,"E72.0");var subQ14=sQuery(id+"F12.wireOp",EDGE,"E72.1");var subQ16=sQuery(id+"F12.wireOp",EDGE,"E74.1");var subQ18=sQuery(id+"F12.wireOp",EDGE,"E74.8");Q0=qUnion([makeQuery(id+"F12.imprint","IMPRINT",FACE,{"disambiguationData":[TD([[makeQuery(id+"F12.imprint","IMPRINT",EDGE,{"derivedFrom":subQ7}),1.0]])]}),makeQuery(id+"F12.imprint","IMPRINT",FACE,{"disambiguationData":[TD([[makeQuery(id+"F12.imprint","IMPRINT",EDGE,{"derivedFrom":subQ14}),1.0]])]}),makeQuery(id+"F12.imprint","IMPRINT",FACE,{"disambiguationData":[TD([[makeQuery(id+"F12.imprint","IMPRINT",EDGE,{"derivedFrom":subQ16}),1.0]])]}),makeQuery(id+"F12.imprint","IMPRINT",FACE,{"disambiguationData":[TD([[makeQuery(id+"F12.imprint","IMPRINT",EDGE,{"derivedFrom":subQ18}),-1.0]])]})]);}
            var Q1;
            Q1=makeQuery(id+"F5.boolean.opBoolean","SPLIT",FACE,{"disambiguationData":[TD([makeQuery(id+"F5.opExtrude","SWEPT_FACE",FACE,{"disambiguationData":[OSD([sQuery(id+"F4.wireOp",EDGE,"E41")])]})])],"derivedFrom":makeQuery(id+"F3.boolean.opBoolean","COPY",FACE,{"derivedFrom":makeQuery(id+"F3.opExtrude","CAP_FACE",FACE,{"disambiguationData":[OSD([sQuery(id+"F0.wireOp",EDGE,"E25.0"),sQuery(id+"F0.wireOp",EDGE,"E25.1"),sQuery(id+"F0.wireOp",EDGE,"E25.2"),sQuery(id+"F0.wireOp",EDGE,"E25.3"),sQuery(id+"F0.wireOp",EDGE,"E25.4"),sQuery(id+"F0.wireOp",EDGE,"E25.5"),sQuery(id+"F0.wireOp",EDGE,"E25.6"),sQuery(id+"F0.wireOp",EDGE,"E25.7")])],"isStart":false})})});
            extrude(context, id + "F13", {"entities" : qUnion([Q0]), "operationType" : NewBodyOperationType.REMOVE, "endBound" : BoundingType.UP_TO_SURFACE, "endBoundEntityFace" : qUnion([Q1]), "depth" : 25 * mm});
        }
        {
            var Q0;
            Q0=makeQuery(id+"F3.boolean.opBoolean","COPY",EDGE,{"derivedFrom":makeQuery(id+"F3.opExtrude","CAP_EDGE",EDGE,{"disambiguationData":[OSD([sQuery(id+"F0.wireOp",EDGE,"E25.6")])],"isStart":false})});
            var Q1;
            Q1=makeQuery(id+"F8.boolean.opBoolean","INTERSECT",EDGE,{"derivedFrom":[makeQuery(id+"F5.opExtrude","SWEPT_FACE",FACE,{"disambiguationData":[OSD([sQuery(id+"F4.wireOp",EDGE,"E30")])]}),makeQuery(id+"F8.opExtrude","CAP_FACE",FACE,{"disambiguationData":[OSD([sQuery(id+"F7.wireOp",EDGE,"E67")])],"isStart":false})]});
            var Q2;
            Q2=makeQuery(id+"F8.boolean.opBoolean","INTERSECT",EDGE,{"disambiguationData":[OD(1.0)],"derivedFrom":[makeQuery(id+"F5.opExtrude","SWEPT_FACE",FACE,{"disambiguationData":[OSD([sQuery(id+"F4.wireOp",EDGE,"E30")])]}),makeQuery(id+"F8.opExtrude","SWEPT_FACE",FACE,{"disambiguationData":[OSD([sQuery(id+"F7.wireOp",EDGE,"E67")])]})]});
            var Q3;
            {var subQ0=sQuery(id+"F4.wireOp",EDGE,"E30");Q3=makeQuery(id+"F8.boolean.opBoolean","SPLIT",EDGE,{"disambiguationData":[TD([makeQuery(id+"F5.opExtrude","SWEPT_FACE",FACE,{"disambiguationData":[OSD([sQuery(id+"F4.wireOp",EDGE,"E35.filletArc")])]})])],"derivedFrom":makeQuery(id+"F5.opExtrude","CAP_EDGE",EDGE,{"disambiguationData":[OSD([subQ0])],"isStart":false})});}
            var Q4;
            {var subQ0=sQuery(id+"F0.wireOp",EDGE,"E25.7");var subQ1=sQuery(id+"F0.wireOp",EDGE,"E25.1");var subQ2=sQuery(id+"F0.wireOp",EDGE,"E25.6");var subQ3=sQuery(id+"F0.wireOp",EDGE,"E25.5");var subQ4=sQuery(id+"F0.wireOp",EDGE,"E25.4");var subQ5=sQuery(id+"F0.wireOp",EDGE,"E25.0");var subQ6=sQuery(id+"F0.wireOp",EDGE,"E25.2");var subQ7=sQuery(id+"F0.wireOp",EDGE,"E25.3");Q4=makeQuery(id+"F8.boolean.opBoolean","INTERSECT",EDGE,{"derivedFrom":[makeQuery(id+"F5.boolean.opBoolean","SPLIT",FACE,{"disambiguationData":[TD([makeQuery(id+"F2.opExtrude","SWEPT_FACE",FACE,{"disambiguationData":[OSD([subQ5])]})])],"derivedFrom":makeQuery(id+"F3.boolean.opBoolean","COPY",FACE,{"derivedFrom":makeQuery(id+"F3.opExtrude","CAP_FACE",FACE,{"disambiguationData":[OSD([subQ5,subQ1,subQ6,subQ7,subQ4,subQ3,subQ2,subQ0])],"isStart":false})})}),makeQuery(id+"F8.opExtrude","SWEPT_FACE",FACE,{"disambiguationData":[OSD([sQuery(id+"F7.wireOp",EDGE,"E67")])]})]});}
            var Q5;
            Q5=makeQuery(id+"F8.boolean.opBoolean","INTERSECT",EDGE,{"disambiguationData":[OD(0.0)],"derivedFrom":[makeQuery(id+"F5.opExtrude","SWEPT_FACE",FACE,{"disambiguationData":[OSD([sQuery(id+"F4.wireOp",EDGE,"E30")])]}),makeQuery(id+"F8.opExtrude","SWEPT_FACE",FACE,{"disambiguationData":[OSD([sQuery(id+"F7.wireOp",EDGE,"E67")])]})]});
            fillet(context, id + "F14", {"entities" : qUnion([Q0, Q1, Q2, Q3, Q4, Q5]), "radius" : 3 * mm, "tangentPropagation" : true, "allowEdgeOverflow" : false});
        }
        {
            var Q0;
            Q0=makeQuery(id+"F1.opExtrude","CAP_EDGE",EDGE,{"disambiguationData":[OSD([sQuery(id+"F0.wireOp",EDGE,"E1.bottom")])],"isStart":false});
            fillet(context, id + "F15", {"entities" : qUnion([Q0]), "radius" : 2 * mm, "tangentPropagation" : true, "allowEdgeOverflow" : false});
        }
        {
            var Q0;
            {var subQ0=sQuery(id+"F0.wireOp",EDGE,"E22.filletArc");var subQ1=sQuery(id+"F0.wireOp",EDGE,"E7");var subQ2=sQuery(id+"F0.wireOp",EDGE,"E6");var subQ3=sQuery(id+"F0.wireOp",EDGE,"E5");var subQ4=sQuery(id+"F0.wireOp",EDGE,"E4");var subQ5=sQuery(id+"F0.wireOp",EDGE,"E1.bottom");var subQ6=sQuery(id+"F0.wireOp",EDGE,"E21.filletArc");var subQ7=sQuery(id+"F0.wireOp",EDGE,"E1.top");var subQ8=sQuery(id+"F0.wireOp",EDGE,"E1.left");var subQ9=sQuery(id+"F0.wireOp",EDGE,"E1.right");var subQ10=sQuery(id+"F0.wireOp",EDGE,"E23.filletArc");var subQ11=sQuery(id+"F0.wireOp",EDGE,"E24.filletArc");Q0=makeQuery(id+"F2.boolean.opBoolean","SPLIT",FACE,{"disambiguationData":[TD([makeQuery(id+"F1.opExtrude","SWEPT_FACE",FACE,{"disambiguationData":[OSD([subQ5])]})])],"derivedFrom":makeQuery(id+"F1.opExtrude","CAP_FACE",FACE,{"disambiguationData":[OSD([subQ5,subQ7,subQ8,subQ9,subQ4,subQ3,subQ2,subQ1,subQ6,subQ0,subQ10,subQ11])],"isStart":true})});}
            var sketch = newSketch(context, id + "F16", { "sketchPlane" : qUnion([Q0])});
            skLineSegment(sketch, "E79", {"start": v(-30.66, 74.25) * mm, "end": v(-19.9, 88.3) * mm});
            skLineSegment(sketch, "E80", {"start": v(35.31, 74.25) * mm, "end": v(25.27, 91.16) * mm});
            skLineSegment(sketch, "E81", {"start": v(-19.9, 88.3) * mm, "end": v(-19.9, 102.64) * mm});
            skLineSegment(sketch, "E82", {"start": v(25.27, 91.16) * mm, "end": v(25.27, 106.94) * mm});
            skArc(sketch, "E83", {"start": v(25.27, 106.94) * mm, "mid": v(2, 111.88) * mm, "end": v(-19.9, 102.64) * mm});
            skLineSegment(sketch, "E84", {"start": v(-31.38, -74.25) * mm, "end": v(-24.92, -90.26) * mm});
            skLineSegment(sketch, "E85", {"start": v(24.55, -74.48) * mm, "end": v(16.67, -90.26) * mm});
            skLineSegment(sketch, "E86", {"start": v(16.67, -90.26) * mm, "end": v(16.67, -104.6) * mm});
            skLineSegment(sketch, "E87", {"start": v(-24.92, -90.26) * mm, "end": v(-24.92, -105.32) * mm});
            skArc(sketch, "E88", {"start": v(-24.92, -105.32) * mm, "mid": v(-4.01, -111.86) * mm, "end": v(16.67, -104.6) * mm});
            skSolve(sketch);
        }
        {
            var Q0;
            {var subQ1=sQuery(id+"F16.wireOp",EDGE,"E79");Q0=makeQuery(id+"F16.imprint","IMPRINT",FACE,{"disambiguationData":[TD([[makeQuery(id+"F16.imprint","IMPRINT",EDGE,{"derivedFrom":subQ1}),-1.0]])]});}
            extrude(context, id + "F17", {"entities" : qUnion([Q0]), "depth" : .1 * mm});
        }
        {
            var Q0;
            {var subQ0=sQuery(id+"F0.wireOp",EDGE,"E22.filletArc");var subQ1=sQuery(id+"F0.wireOp",EDGE,"E7");var subQ2=sQuery(id+"F0.wireOp",EDGE,"E6");var subQ3=sQuery(id+"F0.wireOp",EDGE,"E5");var subQ4=sQuery(id+"F0.wireOp",EDGE,"E4");var subQ5=sQuery(id+"F0.wireOp",EDGE,"E1.bottom");var subQ6=sQuery(id+"F0.wireOp",EDGE,"E21.filletArc");var subQ7=sQuery(id+"F0.wireOp",EDGE,"E1.top");var subQ8=sQuery(id+"F0.wireOp",EDGE,"E1.left");var subQ9=sQuery(id+"F0.wireOp",EDGE,"E1.right");var subQ10=sQuery(id+"F0.wireOp",EDGE,"E23.filletArc");var subQ11=sQuery(id+"F0.wireOp",EDGE,"E24.filletArc");Q0=makeQuery(id+"F2.boolean.opBoolean","SPLIT",FACE,{"disambiguationData":[TD([makeQuery(id+"F1.opExtrude","SWEPT_FACE",FACE,{"disambiguationData":[OSD([subQ5])]})])],"derivedFrom":makeQuery(id+"F1.opExtrude","CAP_FACE",FACE,{"disambiguationData":[OSD([subQ5,subQ7,subQ8,subQ9,subQ4,subQ3,subQ2,subQ1,subQ6,subQ0,subQ10,subQ11])],"isStart":true})});}
            var sketch = newSketch(context, id + "F18", { "sketchPlane" : qUnion([Q0])});
            skLineSegment(sketch, "E89", {"start": v(-28.42, -74.25) * mm, "end": v(-15.12, -86.46) * mm});
            skLineSegment(sketch, "E90", {"start": v(25.59, -74.25) * mm, "end": v(18.54, -88.02) * mm});
            skLineSegment(sketch, "E91", {"start": v(18.54, -88.02) * mm, "end": v(18.54, -102.11) * mm});
            skLineSegment(sketch, "E92", {"start": v(-15.12, -86.46) * mm, "end": v(-15.12, -105.25) * mm});
            skArc(sketch, "E93", {"start": v(-15.12, -105.25) * mm, "mid": v(2.2, -108.9) * mm, "end": v(18.54, -102.11) * mm});
            skSolve(sketch);
        }
        {
            var Q0;
            {var subQ1=sQuery(id+"F18.wireOp",EDGE,"E89");Q0=makeQuery(id+"F18.imprint","IMPRINT",FACE,{"disambiguationData":[TD([[makeQuery(id+"F18.imprint","IMPRINT",EDGE,{"derivedFrom":subQ1}),1.0]])]});}
            extrude(context, id + "F19", {"entities" : qUnion([Q0]), "depth" : .10 * mm});
        }
    });
